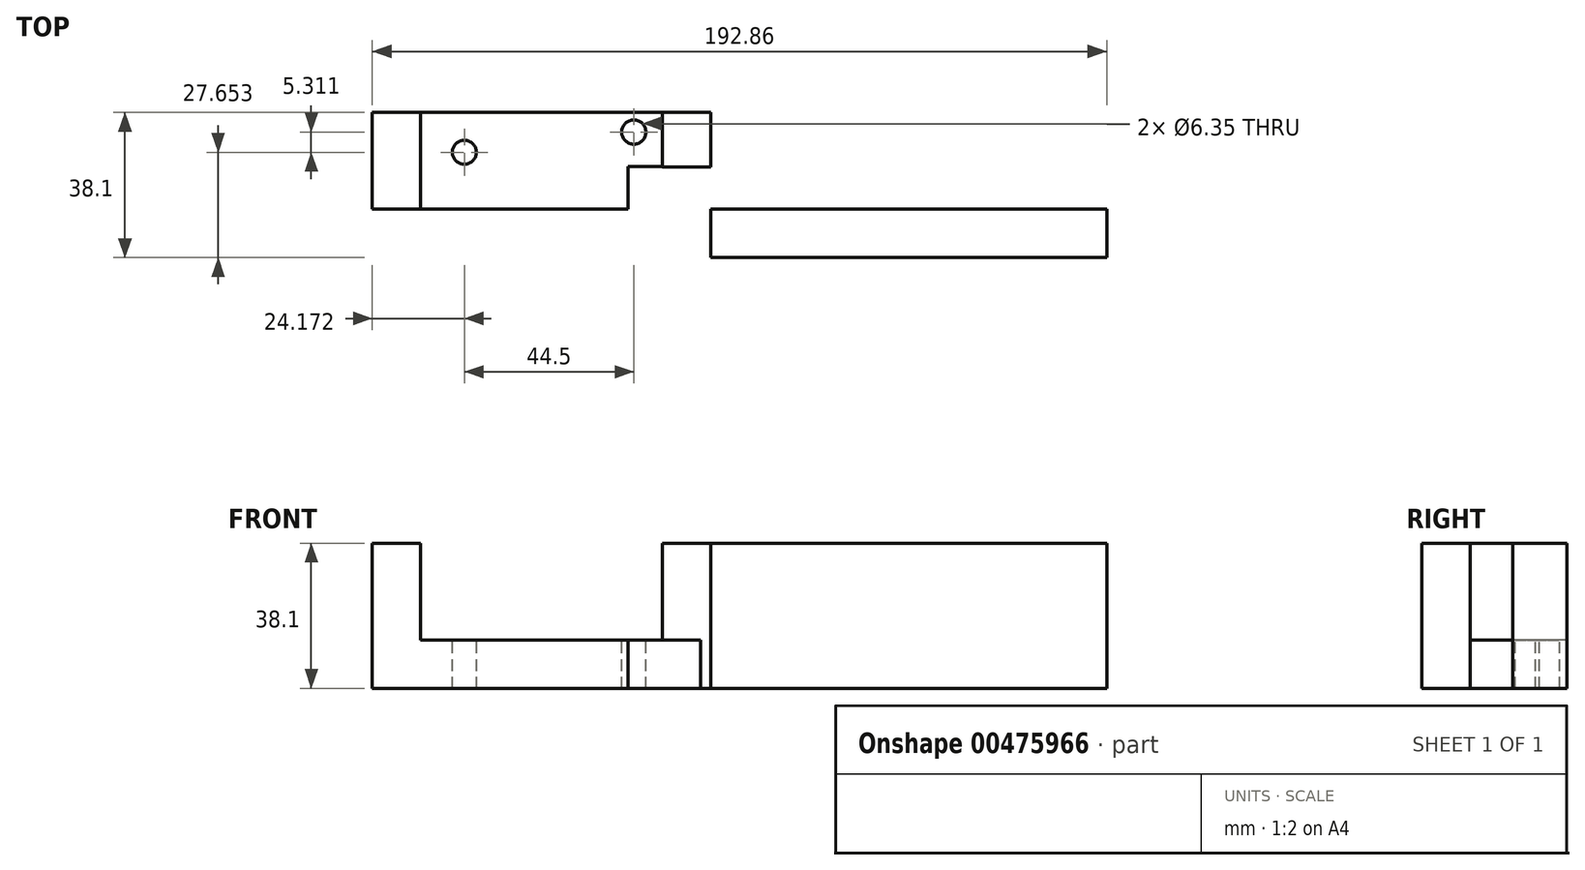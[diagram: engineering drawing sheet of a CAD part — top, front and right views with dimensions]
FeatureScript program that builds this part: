
annotation { "Feature Type Name" : "Feature", "Feature Type Description" : "" }
export const myFeature = defineFeature(function(context is Context, id is Id, definition is map)
    precondition{}
    {
        {
            var Q0;
            Q0=qCreatedBy(makeId("Front.planeOp"),FACE);
            var sketch = newSketch(context, id + "F0", { "sketchPlane" : qUnion([Q0])});
            skLineSegment(sketch, "E0.bottom", {"start": v(-44.45, -25.4) * mm, "end": v(44.45, -25.4) * mm});
            skLineSegment(sketch, "E0.top", {"start": v(-44.45, 25.4) * mm, "end": v(44.45, 25.4) * mm});
            skLineSegment(sketch, "E0.left", {"start": v(-44.45, -25.4) * mm, "end": v(-44.45, 25.4) * mm});
            skLineSegment(sketch, "E0.right", {"start": v(44.45, -25.4) * mm, "end": v(44.45, 25.4) * mm});
            skPoint(sketch, "E0.middle", {"position": v(0, 0) * mm});
            skSolve(sketch);
        }
        {
            var Q0;
            Q0 = qSketchRegion(id + "F0", true);
            extrude(context, id + "F1", {"entities" : qUnion([Q0]), "depth" : 25.4 * mm});
        }
        {
            var Q0;
            Q0=makeQuery(id+"F1.opExtrude","CAP_FACE",FACE,{"disambiguationData":[OSD([sQuery(id+"F0.wireOp",EDGE,"E0.bottom"),sQuery(id+"F0.wireOp",EDGE,"E0.top"),sQuery(id+"F0.wireOp",EDGE,"E0.left"),sQuery(id+"F0.wireOp",EDGE,"E0.right")])],"isStart":false});
            var sketch = newSketch(context, id + "F2", { "sketchPlane" : qUnion([Q0])});
            skLineSegment(sketch, "E1.bottom", {"start": v(-31.75, 25.4) * mm, "end": v(31.75, 25.4) * mm});
            skLineSegment(sketch, "E1.top", {"start": v(-31.75, 0) * mm, "end": v(31.75, 0) * mm});
            skLineSegment(sketch, "E1.left", {"start": v(-31.75, 25.4) * mm, "end": v(-31.75, 0) * mm});
            skLineSegment(sketch, "E1.right", {"start": v(31.75, 25.4) * mm, "end": v(31.75, 0) * mm});
            skSolve(sketch);
        }
        {
            var Q0;
            Q0=makeQuery(id+"F2.imprint","IMPRINT",FACE,{"disambiguationData":[TD([[makeQuery(id+"F2.imprint","IMPRINT",EDGE,{"derivedFrom":sQuery(id+"F2.wireOp",EDGE,"E1.bottom")}),-1.0]])]});
            extrude(context, id + "F3", {"entities" : qUnion([Q0]), "operationType" : NewBodyOperationType.REMOVE, "endBound" : BoundingType.THROUGH_ALL, "oppositeDirection" : true, "depth" : 25.4 * mm});
        }
        {
            var Q0;
            Q0=makeQuery(id+"F1.opExtrude","CAP_FACE",FACE,{"disambiguationData":[OSD([sQuery(id+"F0.wireOp",EDGE,"E0.bottom"),sQuery(id+"F0.wireOp",EDGE,"E0.top"),sQuery(id+"F0.wireOp",EDGE,"E0.left"),sQuery(id+"F0.wireOp",EDGE,"E0.right")])],"isStart":false});
            var sketch = newSketch(context, id + "F4", { "sketchPlane" : qUnion([Q0])});
            skLineSegment(sketch, "E2.bottom", {"start": v(-44.45, -12.7) * mm, "end": v(44.45, -12.7) * mm});
            skLineSegment(sketch, "E2.top", {"start": v(-44.45, -25.4) * mm, "end": v(44.45, -25.4) * mm});
            skLineSegment(sketch, "E2.left", {"start": v(-44.45, -12.7) * mm, "end": v(-44.45, -25.4) * mm});
            skLineSegment(sketch, "E2.right", {"start": v(44.45, -12.7) * mm, "end": v(44.45, -25.4) * mm});
            skSolve(sketch);
        }
        {
            var Q0;
            Q0 = qSketchRegion(id + "F4", true);
            extrude(context, id + "F5", {"entities" : qUnion([Q0]), "operationType" : NewBodyOperationType.REMOVE, "endBound" : BoundingType.THROUGH_ALL, "oppositeDirection" : true, "depth" : 25.4 * mm});
        }
        {
            var Q0;
            Q0=makeQuery(id+"F1.opExtrude","SWEPT_FACE",FACE,{"disambiguationData":[OSD([sQuery(id+"F0.wireOp",EDGE,"E0.right")])]});
            var sketch = newSketch(context, id + "F6", { "sketchPlane" : qUnion([Q0])});
            skLineSegment(sketch, "E3.bottom", {"start": v(-25.4, 25.4) * mm, "end": v(-38.1, 25.4) * mm});
            skLineSegment(sketch, "E3.top", {"start": v(-25.4, -12.7) * mm, "end": v(-38.1, -12.7) * mm});
            skLineSegment(sketch, "E3.left", {"start": v(-25.4, 25.4) * mm, "end": v(-25.4, -12.7) * mm});
            skLineSegment(sketch, "E3.right", {"start": v(-38.1, 25.4) * mm, "end": v(-38.1, -12.7) * mm});
            skSolve(sketch);
        }
        {
            var Q0;
            Q0=makeQuery(id+"F6.imprint","IMPRINT",FACE,{"disambiguationData":[TD([[makeQuery(id+"F6.imprint","IMPRINT",EDGE,{"derivedFrom":sQuery(id+"F6.wireOp",EDGE,"E3.bottom")}),1.0]])]});
            extrude(context, id + "F7", {"entities" : qUnion([Q0]), "operationType" : NewBodyOperationType.ADD, "endBound" : BoundingType.THROUGH_ALL, "depth" : 25.4 * mm});
        }
        {
            var Q0;
            Q0=makeQuery(id+"F3.boolean.opBoolean","COPY",FACE,{"derivedFrom":makeQuery(id+"F3.opExtrude","SWEPT_FACE",FACE,{"disambiguationData":[OSD([sQuery(id+"F2.wireOp",EDGE,"E1.top")])]})});
            var sketch = newSketch(context, id + "F8", { "sketchPlane" : qUnion([Q0])});
            skLineSegment(sketch, "E4.bottom", {"start": v(41.79, -25.59) * mm, "end": v(22.74, -25.59) * mm});
            skLineSegment(sketch, "E4.top", {"start": v(41.79, -14.14) * mm, "end": v(22.74, -14.14) * mm});
            skLineSegment(sketch, "E4.left", {"start": v(41.79, -25.59) * mm, "end": v(41.79, -14.14) * mm});
            skLineSegment(sketch, "E4.right", {"start": v(22.74, -25.59) * mm, "end": v(22.74, -14.14) * mm});
            skSolve(sketch);
        }
        {
            var Q0;
            Q0 = qSketchRegion(id + "F8", true);
            extrude(context, id + "F9", {"entities" : qUnion([Q0]), "operationType" : NewBodyOperationType.REMOVE, "endBound" : BoundingType.THROUGH_ALL, "oppositeDirection" : true, "depth" : 25.4 * mm});
        }
        {
            var Q0;
            {var subQ0=sQuery(id+"F0.wireOp",EDGE,"E0.right");var subQ2=sQuery(id+"F0.wireOp",EDGE,"E0.top");Q0=makeQuery(id+"F3.boolean.opBoolean","SPLIT",FACE,{"disambiguationData":[TD([makeQuery(id+"F1.opExtrude","SWEPT_FACE",FACE,{"disambiguationData":[OSD([subQ0])]})])],"derivedFrom":makeQuery(id+"F1.opExtrude","SWEPT_FACE",FACE,{"disambiguationData":[OSD([subQ2])]})});}
            var sketch = newSketch(context, id + "F10", { "sketchPlane" : qUnion([Q0])});
            skLineSegment(sketch, "E5.bottom", {"start": v(44.45, -25.4) * mm, "end": v(31.75, -25.4) * mm});
            skLineSegment(sketch, "E5.top", {"start": v(44.45, -14.3) * mm, "end": v(31.75, -14.3) * mm});
            skLineSegment(sketch, "E5.left", {"start": v(44.45, -25.4) * mm, "end": v(44.45, -14.3) * mm});
            skLineSegment(sketch, "E5.right", {"start": v(31.75, -25.4) * mm, "end": v(31.75, -14.3) * mm});
            skSolve(sketch);
        }
        {
            var Q0;
            Q0 = qSketchRegion(id + "F10", true);
            extrude(context, id + "F11", {"entities" : qUnion([Q0]), "operationType" : NewBodyOperationType.REMOVE, "endBound" : BoundingType.THROUGH_ALL, "oppositeDirection" : true, "depth" : 25.4 * mm});
        }
        {
            var Q0;
            Q0=makeQuery(id+"F3.boolean.opBoolean","COPY",FACE,{"derivedFrom":makeQuery(id+"F3.opExtrude","SWEPT_FACE",FACE,{"disambiguationData":[OSD([sQuery(id+"F2.wireOp",EDGE,"E1.top")])]})});
            var sketch = newSketch(context, id + "F12", { "sketchPlane" : qUnion([Q0])});
            skCircle(sketch, "E6", {"center": v(24.22, -5.14) * mm, "radius": 3.18 * mm});
            skSolve(sketch);
        }
        {
            var Q0;
            Q0=makeQuery(id+"F12.imprint","IMPRINT",FACE,{"disambiguationData":[TD([[makeQuery(id+"F12.imprint","IMPRINT",EDGE,{"derivedFrom":sQuery(id+"F12.wireOp",EDGE,"E6")}),-1.0]])]});
            var sketch = newSketch(context, id + "F13", { "sketchPlane" : qUnion([Q0])});
            skCircle(sketch, "E7", {"center": v(-20.28, -10.45) * mm, "radius": 3.18 * mm});
            skSolve(sketch);
        }
        {
            var Q0;
            Q0 = qSketchRegion(id + "F12", true);
            extrude(context, id + "F14", {"entities" : qUnion([Q0]), "operationType" : NewBodyOperationType.REMOVE, "endBound" : BoundingType.THROUGH_ALL, "oppositeDirection" : true, "depth" : 25.4 * mm});
        }
        {
            var Q0;
            Q0=makeQuery(id+"F13.imprint","IMPRINT",FACE,{"disambiguationData":[TD([[makeQuery(id+"F13.imprint","IMPRINT",EDGE,{"derivedFrom":sQuery(id+"F13.wireOp",EDGE,"E7")}),1.0]])]});
            extrude(context, id + "F15", {"entities" : qUnion([Q0]), "operationType" : NewBodyOperationType.REMOVE, "endBound" : BoundingType.THROUGH_ALL, "oppositeDirection" : true, "depth" : 25.4 * mm});
        }
    });
